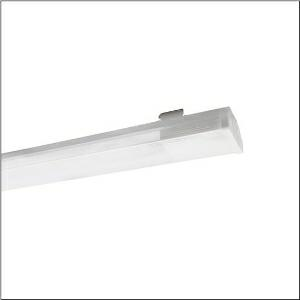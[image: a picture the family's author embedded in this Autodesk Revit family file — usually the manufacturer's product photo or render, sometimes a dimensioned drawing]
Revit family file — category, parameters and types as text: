
# Revit family: modario_31_gen_2_53bm8137u4f5c2_4292
name_source: partatom
category: Lighting Fixtures
units: mm (PartAtom-declared; Revit-internal decimal feet)

## family parameters
Cut with Voids When Loaded = No
Host = Face
Light Source = No
Part Type = Normal
Room Calculation Point = No
Round Connector Dimension = Use Diameter
Shared = No

## types (1)
- Modario 31 Gen.2 (1 x LED, 15990 lm, 90.4 W, 4000K)
    Apparent Load = 90 VA
    CIE Flux Codes = 62 83 95 93 100
    Color Rendering = 80
    Color Temperature = 4000K
    Default Elevation = 1800 mm
    Description = Modario 31 Gen.2, luminaire insert, of sheet steel, coil coated, white, length: 2.392mm, width: 81mm, height: 82mm, 8x system unit, system units: 299mm, LED rated luminous flux: 15.990lm, light colour: 840, SDCM (Standard Deviation of Colour Matching)MacAdam ≤ 3 SDCM (initial), control gear: ON/OFF, with plug, 3-pole, with phase selection, mains connection: 220..240V, AC, 50/60Hz, rated input power: 90W, through-wiring accessed according to module size, primary optical cover: cover, of PMMA, light emission: direct distribution, primary light characteristic: symmetric, protection rating (complete): IP20, protection rating (LED compartment): IP50, insulation class (complete): insulation class I (protective earthing), certification: CE, ENEC, VDE, UKCA, impact resistance: IK03, permissible ambient temperature for indoor applications: -40..+40°C, corresponds to IFS (International Featured Standards) requirements for safety and quality in the food industry, reducing of maximum allowable ambient temperature of 5°C with ceiling mounting, IP40 when using the optional accessory 5TP9018, packaging unit: 1 piece
    Height = 92 mm
    Lamp = 1 x LED
    Lamp Light Flux = 15990 lm
    Lamp Power = 90.4 W
    Lamp count = 1
    Length = 2392 mm
    Luminous efficacy = 177 lm/W
    Manufacturer = Siteco
    ModVariant = No
    Model = 53BM8137U4F5C2
    Mounting Place = Ceiling
    Mounting Type = Pendant
    Number of Poles = 1
    OnlyDefault = Yes
    Power Factor = 1
    Product Name = Modario 31 Gen.2
    Product group = luminaire insert | ceiling pendant
    ProductGroupID = 901
    Protection Class = Protection class I
    Protection Degree = IP 20
    RLX_Detail_Level = 1
    RLX_Emergency_Light_Flux = 0 lm
    RLX_Emergency_Type = 0
    RLX_Emergency_Type_DB = No
    RlxData = <blob elided: 34793 chars, md5=ba86ac0a>
    Socket = socket
    Standby Power = 0 W
    System Light Flux = 15990 lm
    System Power = 90 W
    Type Comments = Product without accessories
    Type Image = l_1341883.jpg
    URL = http://relux.com
    VarID = ---
    Voltage = 0 V
    Weight = 0.00 kg
    Width = 81 mm

## geometry (parser evidence)
native form markers: Blend x4, Sweep x12
no freeform markers — native parametric forms only
